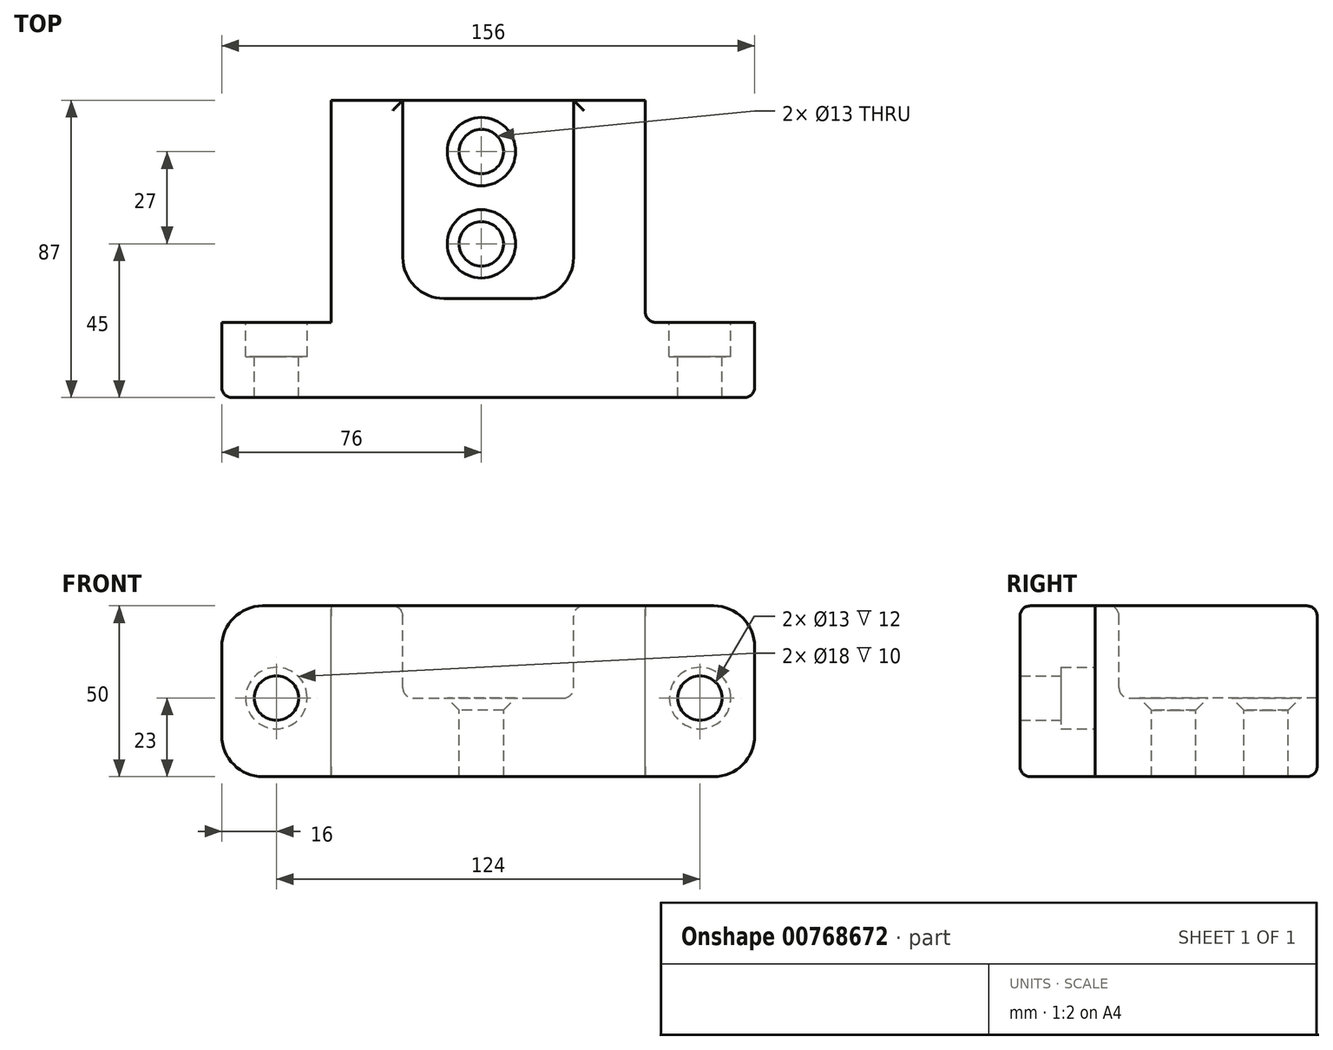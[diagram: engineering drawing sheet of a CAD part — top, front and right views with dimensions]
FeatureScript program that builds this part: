
annotation { "Feature Type Name" : "Feature", "Feature Type Description" : "" }
export const myFeature = defineFeature(function(context is Context, id is Id, definition is map)
    precondition{}
    {
        {
            var Q0;
            Q0=qCreatedBy(makeId("Front.planeOp"),FACE);
            var sketch = newSketch(context, id + "F0", { "sketchPlane" : qUnion([Q0])});
            skLineSegment(sketch, "E0.bottom", {"start": v(0, 0) * mm, "end": v(156, 0) * mm});
            skLineSegment(sketch, "E0.top", {"start": v(0, 50) * mm, "end": v(156, 50) * mm});
            skLineSegment(sketch, "E0.left", {"start": v(0, 0) * mm, "end": v(0, 50) * mm});
            skLineSegment(sketch, "E0.right", {"start": v(156, 0) * mm, "end": v(156, 50) * mm});
            skSolve(sketch);
        }
        {
            var Q0;
            Q0 = qSketchRegion(id + "F0", true);
            extrude(context, id + "F1", {"entities" : qUnion([Q0]), "depth" : 87 * mm, "offsetDistance" : 25 * mm});
        }
        {
            var Q0;
            Q0=makeQuery(id+"F1.opExtrude","SWEPT_FACE",FACE,{"disambiguationData":[OSD([sQuery(id+"F0.wireOp",EDGE,"E0.top")])]});
            var sketch = newSketch(context, id + "F2", { "sketchPlane" : qUnion([Q0])});
            skLineSegment(sketch, "E1.bottom", {"start": v(156, 0) * mm, "end": v(124, 0) * mm});
            skLineSegment(sketch, "E1.top", {"start": v(156, -65) * mm, "end": v(124, -65) * mm});
            skLineSegment(sketch, "E1.left", {"start": v(156, 0) * mm, "end": v(156, -65) * mm});
            skLineSegment(sketch, "E1.right", {"start": v(124, 0) * mm, "end": v(124, -65) * mm});
            skLineSegment(sketch, "E2.bottom", {"start": v(0, 0) * mm, "end": v(32, 0) * mm});
            skLineSegment(sketch, "E2.top", {"start": v(0, -65) * mm, "end": v(32, -65) * mm});
            skLineSegment(sketch, "E2.left", {"start": v(0, 0) * mm, "end": v(0, -65) * mm});
            skLineSegment(sketch, "E2.right", {"start": v(32, 0) * mm, "end": v(32, -65) * mm});
            skSolve(sketch);
        }
        {
            var Q0;
            Q0=makeQuery(id+"F2.imprint","IMPRINT",FACE,{"disambiguationData":[TD([[makeQuery(id+"F2.imprint","IMPRINT",EDGE,{"derivedFrom":sQuery(id+"F2.wireOp",EDGE,"E2.bottom")}),-1.0]])]});
            var Q1;
            Q1=makeQuery(id+"F2.imprint","IMPRINT",FACE,{"disambiguationData":[TD([[makeQuery(id+"F2.imprint","IMPRINT",EDGE,{"derivedFrom":sQuery(id+"F2.wireOp",EDGE,"E1.bottom")}),-1.0]])]});
            extrude(context, id + "F3", {"entities" : qUnion([Q0, Q1]), "operationType" : NewBodyOperationType.REMOVE, "endBound" : BoundingType.UP_TO_NEXT, "oppositeDirection" : true, "depth" : 25 * mm, "offsetDistance" : 25 * mm});
        }
        {
            var Q0;
            Q0=makeQuery(id+"F1.opExtrude","SWEPT_FACE",FACE,{"disambiguationData":[OSD([sQuery(id+"F0.wireOp",EDGE,"E0.top")])]});
            var sketch = newSketch(context, id + "F4", { "sketchPlane" : qUnion([Q0])});
            skLineSegment(sketch, "E3.bottom", {"start": v(53, 0) * mm, "end": v(103, 0) * mm});
            skLineSegment(sketch, "E3.top", {"start": v(53, -58) * mm, "end": v(103, -58) * mm});
            skLineSegment(sketch, "E3.left", {"start": v(53, 0) * mm, "end": v(53, -58) * mm});
            skLineSegment(sketch, "E3.right", {"start": v(103, 0) * mm, "end": v(103, -58) * mm});
            skSolve(sketch);
        }
        {
            var Q0;
            Q0=makeQuery(id+"F4.imprint","IMPRINT",FACE,{"disambiguationData":[TD([[makeQuery(id+"F4.imprint","IMPRINT",EDGE,{"derivedFrom":sQuery(id+"F4.wireOp",EDGE,"E3.bottom")}),-1.0]])]});
            extrude(context, id + "F5", {"entities" : qUnion([Q0]), "operationType" : NewBodyOperationType.REMOVE, "oppositeDirection" : true, "depth" : 27 * mm, "offsetDistance" : 25 * mm});
        }
        {
            var Q0;
            Q0=makeQuery(id+"F3.boolean.opBoolean","COPY",FACE,{"derivedFrom":makeQuery(id+"F3.opExtrude","SWEPT_FACE",FACE,{"disambiguationData":[OSD([sQuery(id+"F2.wireOp",EDGE,"E1.top")])]})});
            var sketch = newSketch(context, id + "F6", { "sketchPlane" : qUnion([Q0])});
            skPoint(sketch, "E4", {"position": v(-140, 23) * mm});
            skPoint(sketch, "E5", {"position": v(-16, 23) * mm});
            skSolve(sketch);
        }
        {
            var Q0;
            Q0=sQuery(id+"F6.wireOp",VERTEX,"E4");
            var Q1;
            Q1=sQuery(id+"F6.wireOp",VERTEX,"E5");
            var Q2;
            Q2=makeQuery(id+"F1.opExtrude","SWEPT_BODY",BODY,{"disambiguationData":[OSD([sQuery(id+"F0.wireOp",EDGE,"E0.bottom"),sQuery(id+"F0.wireOp",EDGE,"E0.top"),sQuery(id+"F0.wireOp",EDGE,"E0.left"),sQuery(id+"F0.wireOp",EDGE,"E0.right")])]});
            hole(context, id + "F7", {"style" : HoleStyle.C_BORE, "endStyle" : HoleEndStyle.THROUGH, "holeDiameter" : 13 * mm, "cBoreDiameter" : 18 * mm, "cBoreDepth" : 10 * mm, "majorDiameter" : 5 * mm, "isTappedThrough" : true, "tappedDepth" : 12 * mm, "tapClearance" : 3, "locations" : qUnion([Q0, Q1]), "scope" : qUnion([Q2])});
        }
        {
            var Q0;
            Q0=makeQuery(id+"F5.boolean.opBoolean","COPY",FACE,{"derivedFrom":makeQuery(id+"F5.opExtrude","CAP_FACE",FACE,{"disambiguationData":[OSD([sQuery(id+"F4.wireOp",EDGE,"E3.bottom"),sQuery(id+"F4.wireOp",EDGE,"E3.top"),sQuery(id+"F4.wireOp",EDGE,"E3.left"),sQuery(id+"F4.wireOp",EDGE,"E3.right")])],"isStart":false})});
            var sketch = newSketch(context, id + "F8", { "sketchPlane" : qUnion([Q0])});
            skPoint(sketch, "E6", {"position": v(76, -15) * mm});
            skPoint(sketch, "E7", {"position": v(76, -42) * mm});
            skSolve(sketch);
        }
        {
            var Q0;
            Q0=sQuery(id+"F8.wireOp",VERTEX,"E6");
            var Q1;
            Q1=sQuery(id+"F8.wireOp",VERTEX,"E7");
            var Q2;
            Q2=makeQuery(id+"F1.opExtrude","SWEPT_BODY",BODY,{"disambiguationData":[OSD([sQuery(id+"F0.wireOp",EDGE,"E0.bottom"),sQuery(id+"F0.wireOp",EDGE,"E0.top"),sQuery(id+"F0.wireOp",EDGE,"E0.left"),sQuery(id+"F0.wireOp",EDGE,"E0.right")])]});
            hole(context, id + "F9", {"style" : HoleStyle.C_SINK, "endStyle" : HoleEndStyle.THROUGH, "holeDiameter" : 13 * mm, "cSinkDiameter" : 20 * mm, "cSinkAngle" : 90 * degree, "majorDiameter" : 5 * mm, "isTappedThrough" : true, "tappedDepth" : 12 * mm, "tapClearance" : 3, "locations" : qUnion([Q0, Q1]), "scope" : qUnion([Q2])});
        }
        {
            var Q0;
            Q0=makeQuery(id+"F1.opExtrude","SWEPT_EDGE",EDGE,{"disambiguationData":[OSD([sQuery(id+"F0.wireOp",EDGE,"E0.top"),sQuery(id+"F0.wireOp",EDGE,"E0.right")])]});
            var Q1;
            Q1=makeQuery(id+"F1.opExtrude","SWEPT_EDGE",EDGE,{"disambiguationData":[OSD([sQuery(id+"F0.wireOp",EDGE,"E0.bottom"),sQuery(id+"F0.wireOp",EDGE,"E0.right")])]});
            var Q2;
            Q2=makeQuery(id+"F1.opExtrude","SWEPT_EDGE",EDGE,{"disambiguationData":[OSD([sQuery(id+"F0.wireOp",EDGE,"E0.top"),sQuery(id+"F0.wireOp",EDGE,"E0.left")])]});
            var Q3;
            Q3=makeQuery(id+"F1.opExtrude","SWEPT_EDGE",EDGE,{"disambiguationData":[OSD([sQuery(id+"F0.wireOp",EDGE,"E0.bottom"),sQuery(id+"F0.wireOp",EDGE,"E0.left")])]});
            var Q4;
            Q4=makeQuery(id+"F5.boolean.opBoolean","COPY",EDGE,{"derivedFrom":makeQuery(id+"F5.opExtrude","SWEPT_EDGE",EDGE,{"disambiguationData":[OSD([sQuery(id+"F4.wireOp",EDGE,"E3.top"),sQuery(id+"F4.wireOp",EDGE,"E3.right")])]})});
            var Q5;
            Q5=makeQuery(id+"F5.boolean.opBoolean","COPY",EDGE,{"derivedFrom":makeQuery(id+"F5.opExtrude","SWEPT_EDGE",EDGE,{"disambiguationData":[OSD([sQuery(id+"F4.wireOp",EDGE,"E3.top"),sQuery(id+"F4.wireOp",EDGE,"E3.left")])]})});
            fillet(context, id + "F10", {"entities" : qUnion([Q0, Q1, Q2, Q3, Q4, Q5]), "radius" : 12 * mm, "tangentPropagation" : true, "allowEdgeOverflow" : false});
        }
        {
            var Q0;
            Q0=makeQuery(id+"F1.opExtrude","CAP_EDGE",EDGE,{"disambiguationData":[OSD([sQuery(id+"F0.wireOp",EDGE,"E0.top")])],"isStart":false});
            var Q1;
            Q1=makeQuery(id+"F5.boolean.opBoolean","COPY",EDGE,{"derivedFrom":makeQuery(id+"F5.opExtrude","CAP_EDGE",EDGE,{"disambiguationData":[OSD([sQuery(id+"F4.wireOp",EDGE,"E3.top")])],"isStart":true})});
            var Q2;
            Q2=makeQuery(id+"F5.boolean.opBoolean","COPY",EDGE,{"derivedFrom":makeQuery(id+"F5.opExtrude","CAP_EDGE",EDGE,{"disambiguationData":[OSD([sQuery(id+"F4.wireOp",EDGE,"E3.left")])],"isStart":true})});
            var Q3;
            Q3=makeQuery(id+"F5.boolean.opBoolean","COPY",EDGE,{"derivedFrom":makeQuery(id+"F5.opExtrude","CAP_EDGE",EDGE,{"disambiguationData":[OSD([sQuery(id+"F4.wireOp",EDGE,"E3.right")])],"isStart":true})});
            var Q4;
            Q4=makeQuery(id+"F10.opFillet","BLEND_EDGE",EDGE,{"blendedFrom":[makeQuery(id+"F5.boolean.opBoolean","COPY",EDGE,{"derivedFrom":makeQuery(id+"F5.opExtrude","SWEPT_EDGE",EDGE,{"disambiguationData":[OSD([sQuery(id+"F4.wireOp",EDGE,"E3.top"),sQuery(id+"F4.wireOp",EDGE,"E3.left")])]})}),makeQuery(id+"F1.opExtrude","SWEPT_FACE",FACE,{"disambiguationData":[OSD([sQuery(id+"F0.wireOp",EDGE,"E0.top")])]})],"blendedInto":[makeQuery(id+"F1.opExtrude","SWEPT_FACE",FACE,{"disambiguationData":[OSD([sQuery(id+"F0.wireOp",EDGE,"E0.top")])]})]});
            var Q5;
            Q5=makeQuery(id+"F10.opFillet","BLEND_EDGE",EDGE,{"blendedFrom":[makeQuery(id+"F5.boolean.opBoolean","COPY",EDGE,{"derivedFrom":makeQuery(id+"F5.opExtrude","SWEPT_EDGE",EDGE,{"disambiguationData":[OSD([sQuery(id+"F4.wireOp",EDGE,"E3.top"),sQuery(id+"F4.wireOp",EDGE,"E3.right")])]})}),makeQuery(id+"F1.opExtrude","SWEPT_FACE",FACE,{"disambiguationData":[OSD([sQuery(id+"F0.wireOp",EDGE,"E0.top")])]})],"blendedInto":[makeQuery(id+"F1.opExtrude","SWEPT_FACE",FACE,{"disambiguationData":[OSD([sQuery(id+"F0.wireOp",EDGE,"E0.top")])]})]});
            var Q6;
            Q6=makeQuery(id+"F3.boolean.opBoolean","COPY",EDGE,{"derivedFrom":makeQuery(id+"F3.opExtrude","CAP_EDGE",EDGE,{"disambiguationData":[OSD([sQuery(id+"F2.wireOp",EDGE,"E1.right")])],"isStart":true})});
            var Q7;
            Q7=makeQuery(id+"F3.boolean.opBoolean","COPY",EDGE,{"derivedFrom":makeQuery(id+"F3.opExtrude","CAP_EDGE",EDGE,{"disambiguationData":[OSD([sQuery(id+"F2.wireOp",EDGE,"E1.top")])],"isStart":true})});
            var Q8;
            Q8=makeQuery(id+"F3.boolean.opBoolean","COPY",EDGE,{"derivedFrom":makeQuery(id+"F3.opExtrude","SWEPT_EDGE",EDGE,{"disambiguationData":[OSD([sQuery(id+"F2.wireOp",EDGE,"E1.top"),sQuery(id+"F2.wireOp",EDGE,"E1.right")])]})});
            var Q9;
            Q9=makeQuery(id+"F3.boolean.opBoolean","COPY",EDGE,{"derivedFrom":makeQuery(id+"F3.opExtrude","SWEPT_EDGE",EDGE,{"disambiguationData":[OSD([sQuery(id+"F0.wireOp",EDGE,"E0.top"),sQuery(id+"F2.wireOp",EDGE,"E1.bottom"),sQuery(id+"F2.wireOp",EDGE,"E1.right")])]})});
            var Q10;
            Q10=makeQuery(id+"F5.boolean.opBoolean","COPY",EDGE,{"derivedFrom":makeQuery(id+"F5.opExtrude","CAP_EDGE",EDGE,{"disambiguationData":[OSD([sQuery(id+"F4.wireOp",EDGE,"E3.bottom")])],"isStart":false})});
            var Q11;
            Q11=makeQuery(id+"F5.boolean.opBoolean","COPY",EDGE,{"derivedFrom":makeQuery(id+"F5.opExtrude","CAP_EDGE",EDGE,{"disambiguationData":[OSD([sQuery(id+"F4.wireOp",EDGE,"E3.left")])],"isStart":false})});
            var Q12;
            {var subQ0=sQuery(id+"F4.wireOp",EDGE,"E3.left");var subQ1=sQuery(id+"F4.wireOp",EDGE,"E3.top");Q12=makeQuery(id+"F10.opFillet","BLEND_EDGE",EDGE,{"blendedFrom":[makeQuery(id+"F5.boolean.opBoolean","COPY",EDGE,{"derivedFrom":makeQuery(id+"F5.opExtrude","SWEPT_EDGE",EDGE,{"disambiguationData":[OSD([subQ1,subQ0])]})}),makeQuery(id+"F5.boolean.opBoolean","COPY",FACE,{"derivedFrom":makeQuery(id+"F5.opExtrude","CAP_FACE",FACE,{"disambiguationData":[OSD([sQuery(id+"F4.wireOp",EDGE,"E3.bottom"),subQ1,subQ0,sQuery(id+"F4.wireOp",EDGE,"E3.right")])],"isStart":false})})],"blendedInto":[makeQuery(id+"F5.boolean.opBoolean","COPY",FACE,{"derivedFrom":makeQuery(id+"F5.opExtrude","CAP_FACE",FACE,{"disambiguationData":[OSD([sQuery(id+"F4.wireOp",EDGE,"E3.bottom"),subQ1,subQ0,sQuery(id+"F4.wireOp",EDGE,"E3.right")])],"isStart":false})})]});}
            var Q13;
            Q13=makeQuery(id+"F1.opExtrude","CAP_EDGE",EDGE,{"disambiguationData":[OSD([sQuery(id+"F0.wireOp",EDGE,"E0.bottom")])],"isStart":true});
            var Q14;
            Q14=makeQuery(id+"F3.boolean.opBoolean","COPY",EDGE,{"derivedFrom":makeQuery(id+"F3.opExtrude","SWEPT_EDGE",EDGE,{"disambiguationData":[OSD([sQuery(id+"F0.wireOp",EDGE,"E0.top"),sQuery(id+"F2.wireOp",EDGE,"E2.bottom"),sQuery(id+"F2.wireOp",EDGE,"E2.right")])]})});
            var Q15;
            Q15=makeQuery(id+"F3.boolean.opBoolean","COPY",EDGE,{"derivedFrom":makeQuery(id+"F3.opExtrude","CAP_EDGE",EDGE,{"disambiguationData":[OSD([sQuery(id+"F2.wireOp",EDGE,"E2.right")])],"isStart":true})});
            var Q16;
            Q16=makeQuery(id+"F1.opExtrude","CAP_EDGE",EDGE,{"disambiguationData":[OSD([sQuery(id+"F0.wireOp",EDGE,"E0.bottom")])],"isStart":false});
            var Q17;
            Q17=makeQuery(id+"F3.boolean.opBoolean","COPY",EDGE,{"derivedFrom":makeQuery(id+"F3.opExtrude","CAP_EDGE",EDGE,{"disambiguationData":[OSD([sQuery(id+"F2.wireOp",EDGE,"E2.right")])],"isStart":false})});
            var Q18;
            {var subQ0=sQuery(id+"F0.wireOp",EDGE,"E0.top");Q18=makeQuery(id+"F5.boolean.opBoolean","SPLIT",EDGE,{"disambiguationData":[TD([makeQuery(id+"F3.boolean.opBoolean","COPY",FACE,{"derivedFrom":makeQuery(id+"F3.opExtrude","SWEPT_FACE",FACE,{"disambiguationData":[OSD([sQuery(id+"F2.wireOp",EDGE,"E1.right")])]})})])],"derivedFrom":makeQuery(id+"F1.opExtrude","CAP_EDGE",EDGE,{"disambiguationData":[OSD([subQ0])],"isStart":true})});}
            var Q19;
            {var subQ0=sQuery(id+"F0.wireOp",EDGE,"E0.top");Q19=makeQuery(id+"F5.boolean.opBoolean","SPLIT",EDGE,{"disambiguationData":[TD([makeQuery(id+"F3.boolean.opBoolean","COPY",FACE,{"derivedFrom":makeQuery(id+"F3.opExtrude","SWEPT_FACE",FACE,{"disambiguationData":[OSD([sQuery(id+"F2.wireOp",EDGE,"E2.right")])]})})])],"derivedFrom":makeQuery(id+"F1.opExtrude","CAP_EDGE",EDGE,{"disambiguationData":[OSD([subQ0])],"isStart":true})});}
            var Q20;
            Q20=makeQuery(id+"F3.boolean.opBoolean","COPY",EDGE,{"derivedFrom":makeQuery(id+"F3.opExtrude","CAP_EDGE",EDGE,{"disambiguationData":[OSD([sQuery(id+"F2.wireOp",EDGE,"E1.right")])],"isStart":false})});
            fillet(context, id + "F11", {"entities" : qUnion([Q0, Q1, Q2, Q3, Q4, Q5, Q6, Q7, Q8, Q9, Q10, Q11, Q12, Q13, Q14, Q15, Q16, Q17, Q18, Q19, Q20]), "radius" : 3 * mm, "tangentPropagation" : true, "allowEdgeOverflow" : false});
        }
    });
